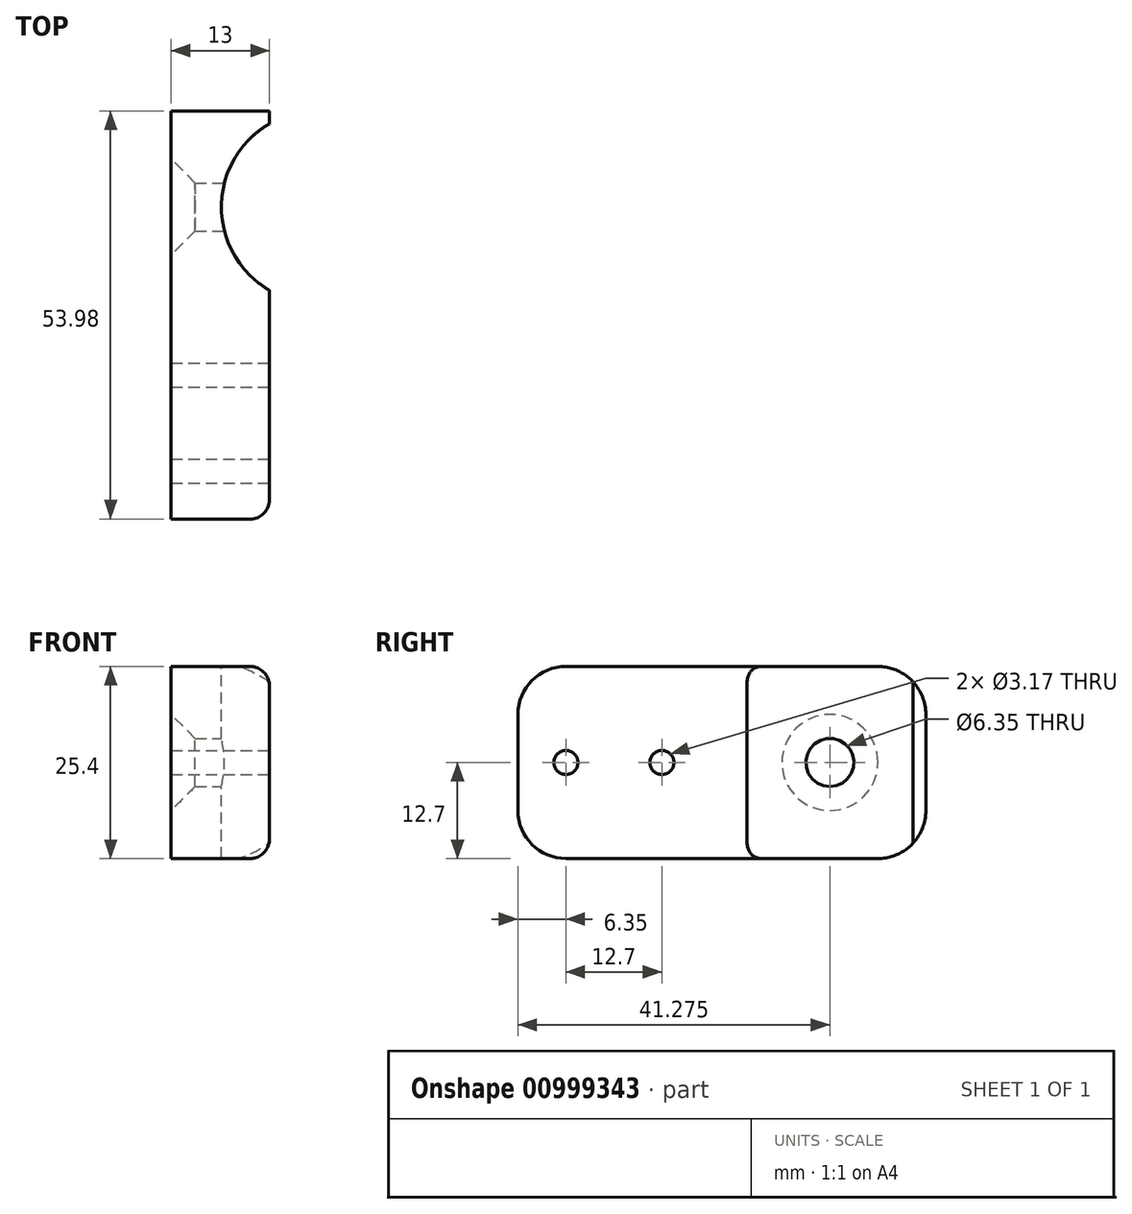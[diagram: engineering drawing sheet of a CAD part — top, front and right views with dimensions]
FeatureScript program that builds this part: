
annotation { "Feature Type Name" : "Feature", "Feature Type Description" : "" }
export const myFeature = defineFeature(function(context is Context, id is Id, definition is map)
    precondition{}
    {
        {
            var Q0;
            Q0=qCreatedBy(makeId("Right.planeOp"),FACE);
            var sketch = newSketch(context, id + "F0", { "sketchPlane" : qUnion([Q0])});
            skLineSegment(sketch, "E0", {"start": v(0, -12.7) * mm, "end": v(53.98, -12.7) * mm});
            skLineSegment(sketch, "E1.MirrorCS", {"start": v(0, 0) * mm, "end": v(0, 12.7) * mm});
            skLineSegment(sketch, "E2.MirrorCS", {"start": v(0, 12.7) * mm, "end": v(53.98, 12.7) * mm});
            skCircle(sketch, "E3.MirrorC", {"center": v(6.35, 0) * mm, "radius": 1.59 * mm});
            skCircle(sketch, "E4", {"center": v(41.27, 0) * mm, "radius": 3.18 * mm});
            skLineSegment(sketch, "E5.MirrorCS", {"start": v(0, 0) * mm, "end": v(0, -12.7) * mm});
            skLineSegment(sketch, "E6", {"start": v(28.57, 12.7) * mm, "end": v(28.57, -12.7) * mm, "construction": true});
            skLineSegment(sketch, "E7", {"start": v(53.98, 12.7) * mm, "end": v(53.98, -12.7) * mm});
            skPoint(sketch, "E8.orphan", {"position": v(92.08, 12.7) * mm});
            skPoint(sketch, "E9.orphan", {"position": v(92.08, -12.7) * mm});
            skCircle(sketch, "E10", {"center": v(19.05, 0) * mm, "radius": 1.59 * mm});
            skCircle(sketch, "E11", {"center": v(19.05, 0) * mm, "radius": 4.45 * mm, "construction": true});
            skCircle(sketch, "E12", {"center": v(6.35, 0) * mm, "radius": 4.45 * mm, "construction": true});
            skCircle(sketch, "E13", {"center": v(19.05, 0) * mm, "radius": 2.41 * mm, "construction": true});
            skSolve(sketch);
        }
        {
            var Q0;
            Q0=qSketchRegion(id+"F0",true);
            extrude(context, id + "F1", {"entities" : qUnion([Q0]), "oppositeDirection" : true, "depth" : 13 * mm, "offsetDistance" : 25 * mm});
        }
        {
            var Q0;
            Q0=qCreatedBy(makeId("Top.planeOp"),FACE);
            var sketch = newSketch(context, id + "F2", { "sketchPlane" : qUnion([Q0])});
            skArc(sketch, "E14", {"start": v(0, 52.27) * mm, "mid": v(-6.35, 41.27) * mm, "end": v(0, 30.28) * mm});
            skLineSegment(sketch, "E15", {"start": v(0, 30.28) * mm, "end": v(0, 52.27) * mm});
            skSolve(sketch);
        }
        {
            var Q0;
            Q0=qSketchRegion(id+"F2",true);
            extrude(context, id + "F3", {"entities" : qUnion([Q0]), "operationType" : NewBodyOperationType.REMOVE, "endBound" : BoundingType.SYMMETRIC, "oppositeDirection" : true, "depth" : 75 * mm, "offsetDistance" : 25 * mm});
        }
        {
            var Q0;
            Q0=makeQuery(id+"F1.opExtrude","SWEPT_EDGE",EDGE,{"disambiguationData":[OSD([sQuery(id+"F0.wireOp",EDGE,"d868d885-708a-4358-ac4c-7e472c41f0fd2.MirrorCS"),sQuery(id+"F0.wireOp",EDGE,"d868d885-708a-4358-ac4c-7e472c41f0fd4.MirrorCS")])]});
            var Q1;
            Q1=makeQuery(id+"F1.opExtrude","SWEPT_EDGE",EDGE,{"disambiguationData":[OSD([sQuery(id+"F0.wireOp",EDGE,"E2.MirrorCS"),sQuery(id+"F0.wireOp",EDGE,"d868d885-708a-4358-ac4c-7e472c41f0fd4.MirrorCS")])]});
            var Q2;
            Q2=makeQuery(id+"F1.opExtrude","SWEPT_EDGE",EDGE,{"disambiguationData":[OSD([sQuery(id+"F0.wireOp",EDGE,"g0e7l1pj-qA0Y-fhNS-CB5I-AUhqAXy8HTwi"),sQuery(id+"F0.wireOp",EDGE,"E0")])]});
            var Q3;
            Q3=makeQuery(id+"F1.opExtrude","SWEPT_EDGE",EDGE,{"disambiguationData":[OSD([sQuery(id+"F0.wireOp",EDGE,"wscSROFl-acIJ-EUQi-56bg-9ylbmSFamOZR"),sQuery(id+"F0.wireOp",EDGE,"g0e7l1pj-qA0Y-fhNS-CB5I-AUhqAXy8HTwi")])]});
            fillet(context, id + "F4", {"entities" : qUnion([Q0, Q1, Q2, Q3]), "radius" : 6.35 * mm, "tangentPropagation" : true, "defaultsChanged" : true, "vertexSettings" : [], "allowEdgeOverflow" : false});
        }
        {
            var Q0;
            Q0=makeQuery(id+"F1.opExtrude","CAP_EDGE",EDGE,{"disambiguationData":[OSD([sQuery(id+"F0.wireOp",EDGE,"icDlAP6z-lHa9-ogsA-z093-o5SYlzmEFYy4"),sQuery(id+"F0.wireOp",EDGE,"d868d885-708a-4358-ac4c-7e472c41f0fd3.MirrorCS")])],"isStart":false});
            var Q1;
            Q1=makeQuery(id+"F1.opExtrude","CAP_EDGE",EDGE,{"disambiguationData":[OSD([sQuery(id+"F0.wireOp",EDGE,"j31KRHDU-dVKS-fmwK-bgvL-qThiKXJEA8MT"),sQuery(id+"F0.wireOp",EDGE,"E1.MirrorCS")])],"isStart":true});
            var Q2;
            {var subQ0=sQuery(id+"F0.wireOp",EDGE,"E2.MirrorCS");Q2=makeQuery(id+"F3.boolean.opBoolean","SPLIT",EDGE,{"disambiguationData":[TD([makeQuery(id+"F3.opExtrude","SWEPT_FACE",FACE,{"disambiguationData":[OSD([sQuery(id+"F2.wireOp",EDGE,"EOLpYDs0-t0ww-CqrT-IwAT-Zewfj3hZNz2P.top")])]})])],"derivedFrom":makeQuery(id+"F1.opExtrude","CAP_EDGE",EDGE,{"disambiguationData":[OSD([subQ0])],"isStart":true})});}
            var Q3;
            {var subQ0=sQuery(id+"F0.wireOp",EDGE,"E0");Q3=makeQuery(id+"F3.boolean.opBoolean","SPLIT",EDGE,{"disambiguationData":[TD([makeQuery(id+"F3.opExtrude","SWEPT_FACE",FACE,{"disambiguationData":[OSD([sQuery(id+"F2.wireOp",EDGE,"EOLpYDs0-t0ww-CqrT-IwAT-Zewfj3hZNz2P.top")])]})])],"derivedFrom":makeQuery(id+"F1.opExtrude","CAP_EDGE",EDGE,{"disambiguationData":[OSD([subQ0])],"isStart":true})});}
            fillet(context, id + "F5", {"entities" : qUnion([Q0, Q1, Q2, Q3]), "radius" : 2.54 * mm, "tangentPropagation" : true, "defaultsChanged" : false, "vertexSettings" : [], "allowEdgeOverflow" : false});
        }
        {
            var Q0;
            Q0=makeQuery(id+"F1.opExtrude","CAP_EDGE",EDGE,{"disambiguationData":[OSD([sQuery(id+"F0.wireOp",EDGE,"E4")])],"isStart":false});
            chamfer(context, id + "F6", {"entities" : qUnion([Q0]), "width" : 3.17 * mm, "tangentPropagation" : true});
        }
    });
